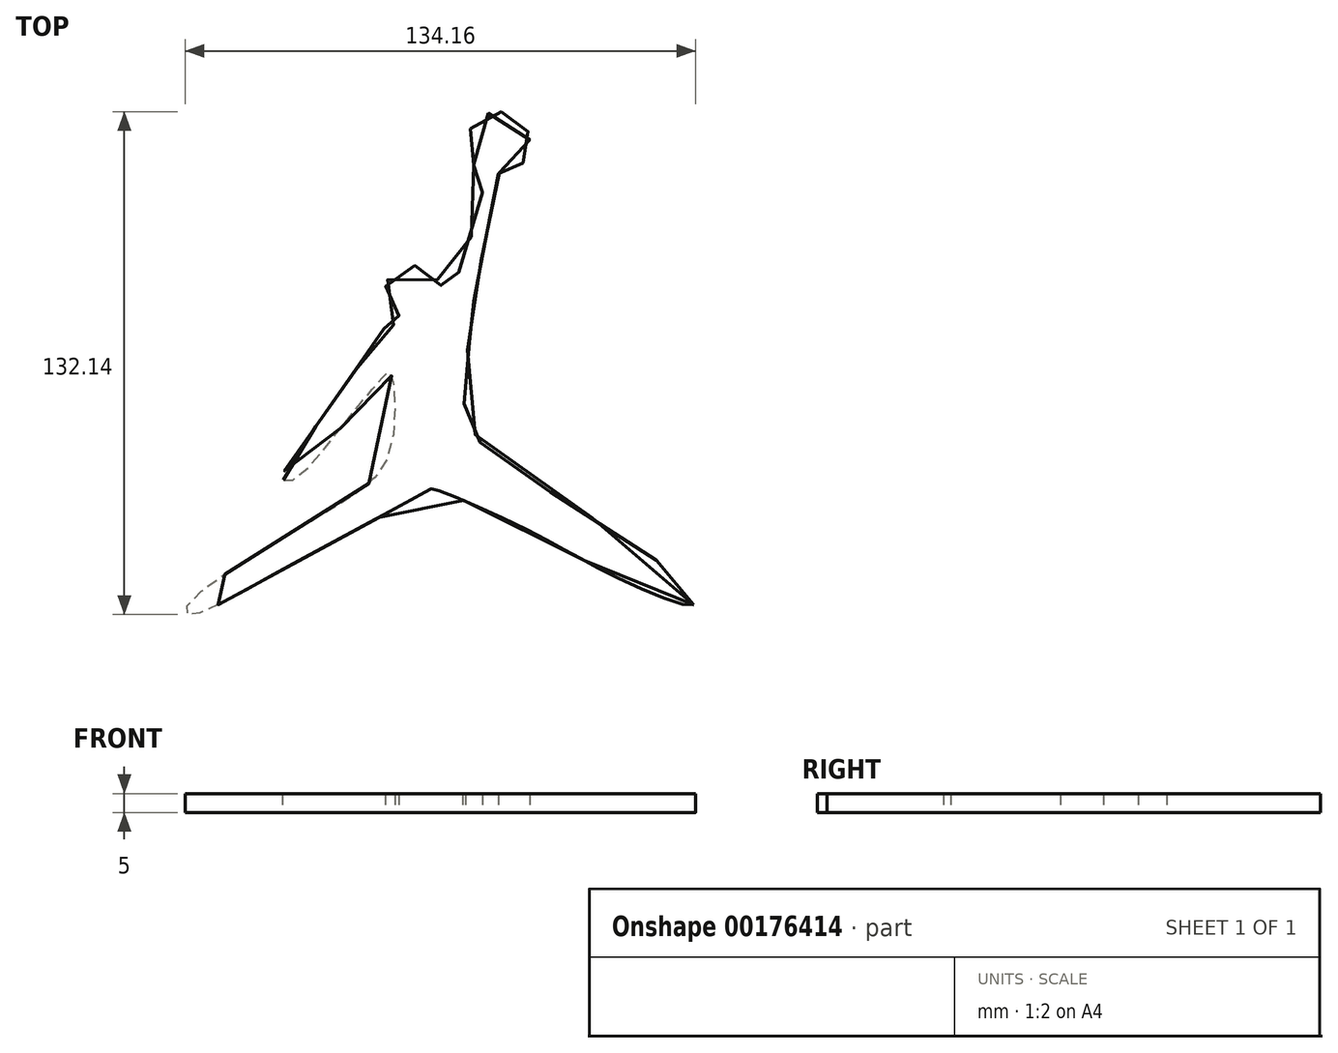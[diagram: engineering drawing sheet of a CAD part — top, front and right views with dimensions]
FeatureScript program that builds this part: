
annotation { "Feature Type Name" : "Feature", "Feature Type Description" : "" }
export const myFeature = defineFeature(function(context is Context, id is Id, definition is map)
    precondition{}
    {
        {
            var Q0;
            Q0=qCreatedBy(makeId("Top.planeOp"),FACE);
            var sketch = newSketch(context, id + "F0", { "sketchPlane" : qUnion([Q0])});
            skFitSpline(sketch, "E0", {"points": [v(65.14, -62.07) * mm, v(59.17, -53.5) * mm, v(11.84, -22.25) * mm, v(6.97, -15.82) * mm, v(4.4, -5.58) * mm, v(6.64, 9.74) * mm, v(6.95, 14.58) * mm, v(12.28, 43) * mm, v(13.75, 50.6) * mm, v(13.85, 51.31) * mm, v(15.8, 51.52) * mm, v(20.08, 53.84) * mm, v(21.94, 58.42) * mm, v(21.32, 62.7) * mm, v(17.82, 66.4) * mm, v(12.36, 67.33) * mm, v(7.41, 64.5) * mm, v(5.25, 58.01) * mm, v(7.82, 52.55) * mm, v(9.06, 49.36) * mm, v(9.36, 44.76) * mm, v(0.46, 19.84) * mm, v(-0.57, 20) * mm, v(-1.5, 22.2) * mm, v(-4.9, 25.97) * mm, v(-10.1, 26.9) * mm, v(-15.3, 23.34) * mm, v(-14.84, 16.18) * mm, v(-12.42, 14.02) * mm, v(-13.14, 12.21) * mm, v(-15.05, 10.51) * mm, v(-16.39, 10.36) * mm, v(-19.94, 5.88) * mm, v(-29.63, -9.27) * mm, v(-42.97, -28.84) * mm, v(-40.53, -29.44) * mm, v(-25.5, -12.93) * mm, v(-16.34, -1.95) * mm, v(-14.8, -0.92) * mm, v(-14.33, -20.24) * mm, v(-29.68, -36.7) * mm, v(-67.9, -62.15) * mm, v(-67.9, -64.6) * mm, v(-42.33, -52.47) * mm, v(-4.95, -32.2) * mm, v(-3.15, -31.73) * mm, v(22.9, -43.22) * mm, v(43.26, -54.1) * mm, v(65.14, -62.07) * mm]});
            skSolve(sketch);
        }
        {
            var Q0;
            Q0=makeQuery(id+"F0.imprint","IMPRINT",FACE,{"disambiguationData":[TD([[makeQuery(id+"F0.imprint","IMPRINT",EDGE,{"derivedFrom":sQuery(id+"F0.wireOp",EDGE,"E0")}),1.0]])]});
            extrude(context, id + "F1", {"entities" : qUnion([Q0]), "depth" : 5 * mm});
        }
    });
